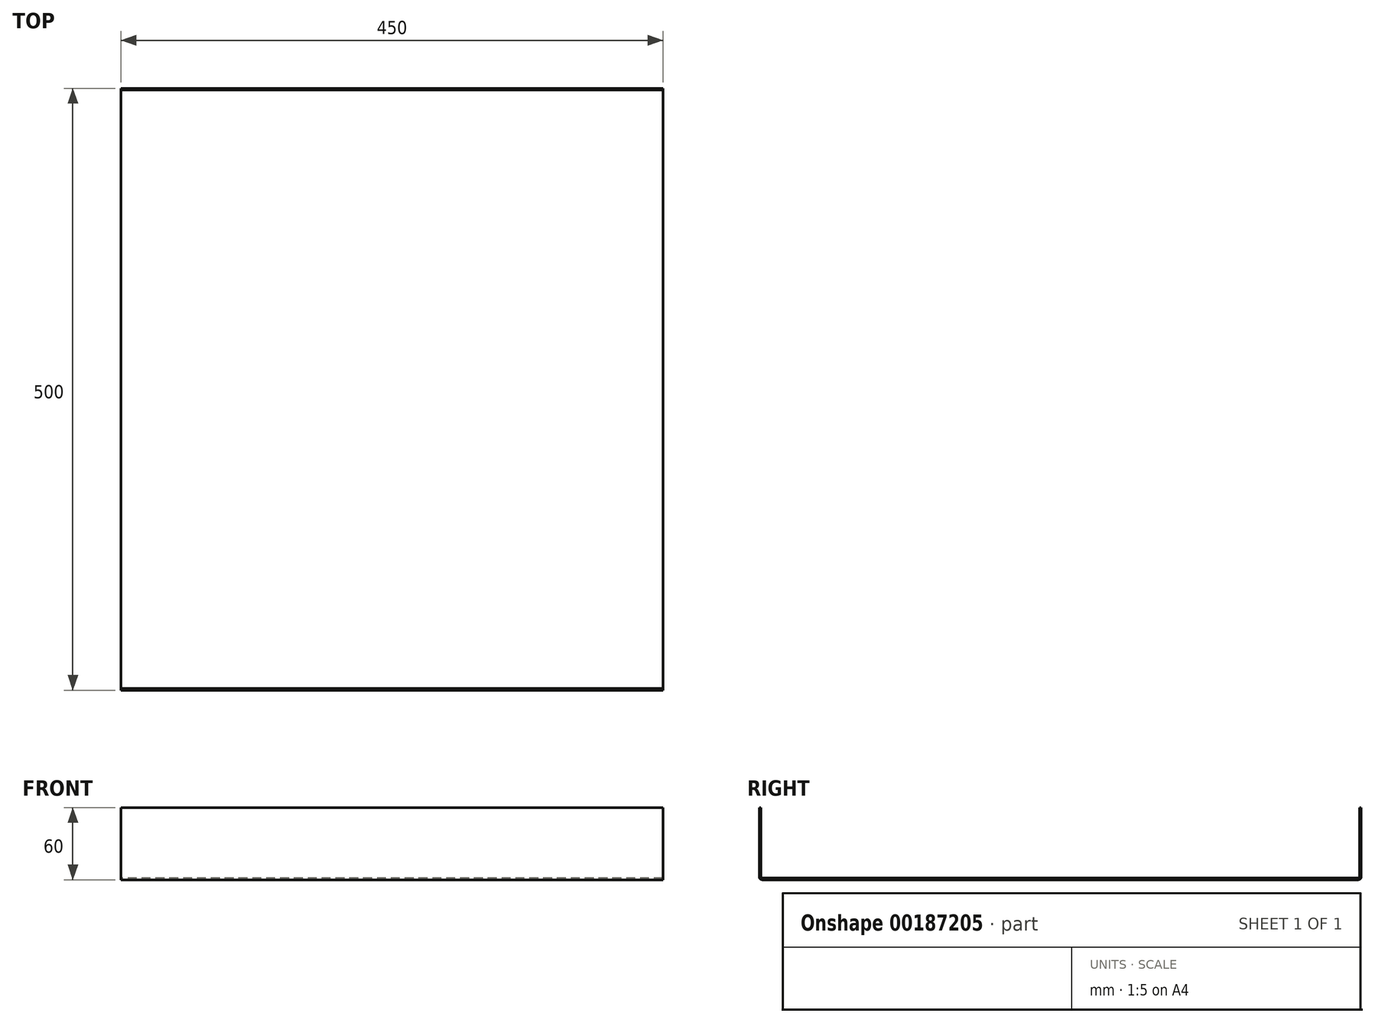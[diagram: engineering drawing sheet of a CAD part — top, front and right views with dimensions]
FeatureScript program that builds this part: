
annotation { "Feature Type Name" : "Feature", "Feature Type Description" : "" }
export const myFeature = defineFeature(function(context is Context, id is Id, definition is map)
    precondition{}
    {
        {
            var Q0;
            Q0=qCreatedBy(makeId("Right.planeOp"),FACE);
            var sketch = newSketch(context, id + "F0", { "sketchPlane" : qUnion([Q0])});
            skLineSegment(sketch, "E0", {"start": v(0, 0) * mm, "end": v(0, -60) * mm});
            skLineSegment(sketch, "E1", {"start": v(0, -60) * mm, "end": v(500, -60) * mm});
            skLineSegment(sketch, "E2", {"start": v(500, -60) * mm, "end": v(500, 0) * mm});
            skLineSegment(sketch, "E3", {"start": v(500, 0) * mm, "end": v(498.5, 0) * mm});
            skLineSegment(sketch, "E4", {"start": v(498.5, 0) * mm, "end": v(498.5, -58.5) * mm});
            skLineSegment(sketch, "E5", {"start": v(498.5, -58.5) * mm, "end": v(1.5, -58.5) * mm});
            skLineSegment(sketch, "E6", {"start": v(1.5, -58.5) * mm, "end": v(1.5, 0) * mm});
            skLineSegment(sketch, "E7", {"start": v(1.5, 0) * mm, "end": v(0, 0) * mm});
            skSolve(sketch);
        }
        {
            var Q0;
            Q0 = qSketchRegion(id + "F0", true);
            extrude(context, id + "F6", {"entities" : qUnion([Q0]), "depth" : 450 * mm});
        }
        {
            var Q0;
            Q0=makeQuery(id+"F6.opExtrude","SWEPT_EDGE",EDGE,{"disambiguationData":[OSD([sQuery(id+"F0.wireOp",EDGE,"E1"),sQuery(id+"F0.wireOp",EDGE,"E2")])]});
            fillet(context, id + "F1", {"entities" : qUnion([Q0]), "radius" : 2.5 * mm, "tangentPropagation" : true, "allowEdgeOverflow" : false});
        }
        {
            var Q0;
            Q0=makeQuery(id+"F6.opExtrude","SWEPT_EDGE",EDGE,{"disambiguationData":[OSD([sQuery(id+"F0.wireOp",EDGE,"E4"),sQuery(id+"F0.wireOp",EDGE,"E5")])]});
            fillet(context, id + "F2", {"entities" : qUnion([Q0]), "radius" : 1.5 * mm, "tangentPropagation" : true, "allowEdgeOverflow" : false});
        }
        {
            var Q0;
            Q0=makeQuery(id+"F6.opExtrude","SWEPT_EDGE",EDGE,{"disambiguationData":[OSD([sQuery(id+"F0.wireOp",EDGE,"E5"),sQuery(id+"F0.wireOp",EDGE,"E6")])]});
            fillet(context, id + "F3", {"entities" : qUnion([Q0]), "radius" : 1.5 * mm, "tangentPropagation" : true, "allowEdgeOverflow" : false});
        }
        {
            var Q0;
            Q0=makeQuery(id+"F6.opExtrude","SWEPT_EDGE",EDGE,{"disambiguationData":[OSD([sQuery(id+"F0.wireOp",EDGE,"E0"),sQuery(id+"F0.wireOp",EDGE,"E1")])]});
            fillet(context, id + "F7", {"entities" : qUnion([Q0]), "radius" : 2.5 * mm, "tangentPropagation" : true, "allowEdgeOverflow" : false});
        }
    });
